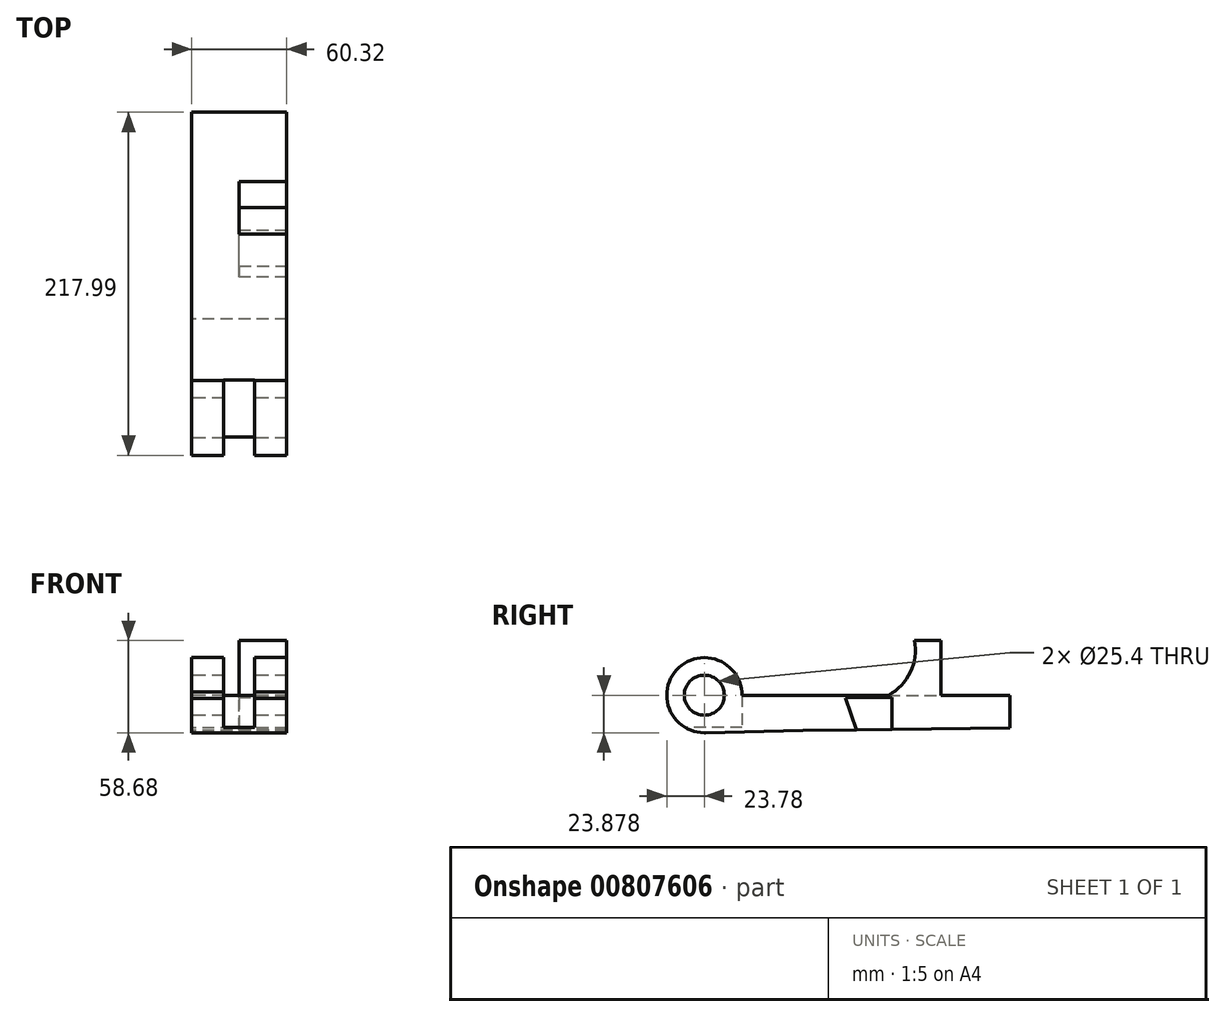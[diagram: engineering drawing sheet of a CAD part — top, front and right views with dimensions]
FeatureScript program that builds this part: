
annotation { "Feature Type Name" : "Feature", "Feature Type Description" : "" }
export const myFeature = defineFeature(function(context is Context, id is Id, definition is map)
    precondition{}
    {
        {
            var Q0;
            Q0=qCreatedBy(makeId("Right.planeOp"),FACE);
            var sketch = newSketch(context, id + "F0", { "sketchPlane" : qUnion([Q0])});
            skLineSegment(sketch, "E0.top", {"start": v(23.88, 20.58) * mm, "end": v(62.76, 20.58) * mm});
            skPoint(sketch, "E1.center.orphan", {"position": v(0, 10.29) * mm});
            skCircle(sketch, "E2", {"center": v(0, 20.58) * mm, "radius": 12.7 * mm});
            skArc(sketch, "E3", {"start": v(23.88, 20.58) * mm, "mid": v(-17.09, 37.25) * mm, "end": v(0.58, -3.3) * mm});
            skLineSegment(sketch, "E4", {"start": v(62.76, -1.77) * mm, "end": v(0, -3.3) * mm});
            skPoint(sketch, "E5.orphan", {"position": v(0, 0) * mm});
            skLineSegment(sketch, "E6", {"start": v(0, 10.29) * mm, "end": v(0, 7.88) * mm});
            skLineSegment(sketch, "E7", {"start": v(117.25, -0.45) * mm, "end": v(117.25, 20.58) * mm});
            skLineSegment(sketch, "E8.trimOffspring", {"start": v(0, -3.3) * mm, "end": v(0, -3.3) * mm});
            skLineSegment(sketch, "E9", {"start": v(0, 20.58) * mm, "end": v(85.85, 20.58) * mm});
            skLineSegment(sketch, "E10", {"start": v(85.85, 20.58) * mm, "end": v(91.86, -1.06) * mm});
            skLineSegment(sketch, "E11.bottom", {"start": v(85.85, 20.58) * mm, "end": v(150.21, 20.58) * mm});
            skLineSegment(sketch, "E11.top", {"start": v(133.54, 55.38) * mm, "end": v(150.21, 55.38) * mm});
            skLineSegment(sketch, "E11.right", {"start": v(150.21, 20.58) * mm, "end": v(150.21, 55.38) * mm});
            skPoint(sketch, "E12.startSnap0", {"position": v(133.54, 55.38) * mm});
            skArc(sketch, "E13", {"start": v(116.86, 20.58) * mm, "mid": v(130.87, 35.26) * mm, "end": v(133.54, 55.38) * mm});
            skPoint(sketch, "E12.start.orphan", {"position": v(133.54, 50.81) * mm});
            skPoint(sketch, "E14.orphan", {"position": v(116.87, 55.38) * mm});
            skLineSegment(sketch, "E15.bottom", {"start": v(23.78, -8.26) * mm, "end": v(-23.78, -8.26) * mm});
            skLineSegment(sketch, "E15.top", {"start": v(23.78, 49.42) * mm, "end": v(-23.78, 49.42) * mm});
            skLineSegment(sketch, "E15.left", {"start": v(23.78, -8.26) * mm, "end": v(23.78, 49.42) * mm});
            skLineSegment(sketch, "E15.right", {"start": v(-23.78, -8.26) * mm, "end": v(-23.78, 49.42) * mm});
            skLineSegment(sketch, "E16", {"start": v(62.76, -1.77) * mm, "end": v(194.2, -0.17) * mm});
            skLineSegment(sketch, "E17", {"start": v(194.2, -0.17) * mm, "end": v(194.2, 20.58) * mm});
            skLineSegment(sketch, "E18", {"start": v(150.21, 20.58) * mm, "end": v(194.2, 20.58) * mm});
            skPoint(sketch, "E19.start.orphan", {"position": v(0, -28.73) * mm});
            skPoint(sketch, "E20.orphan", {"position": v(208.3, 0) * mm});
            skSolve(sketch);
        }
        {
            var Q0;
            Q0=makeQuery(id+"F0.imprint","IMPRINT",FACE,{"disambiguationData":[TD([[makeQuery(id+"F0.imprint","IMPRINT",EDGE,{"derivedFrom":sQuery(id+"F0.wireOp",EDGE,"E11.top")}),-1.0]])]});
            extrude(context, id + "F1", {"entities" : qUnion([Q0]), "depth" : 30.16 * mm, "offsetDistance" : 25.4 * mm});
        }
        {
            var Q0;
            {var subQ5=sQuery(id+"F0.wireOp",EDGE,"E2");var subQ6=makeQuery(id+"F0.imprint","IMPRINT",VERTEX,{"disambiguationData":[OD(0.0)],"derivedFrom":subQ5});Q0=makeQuery(id+"F0.imprint","IMPRINT",FACE,{"disambiguationData":[TD([[makeQuery(id+"F0.imprint","IMPRINT",EDGE,{"disambiguationData":[TD([[subQ6,1.0]])],"derivedFrom":subQ5}),-1.0]])]});}
            var Q1;
            {var subQ9=sQuery(id+"F0.wireOp",EDGE,"E16");Q1=makeQuery(id+"F0.imprint","IMPRINT",FACE,{"disambiguationData":[TD([[makeQuery(id+"F0.imprint","IMPRINT",EDGE,{"derivedFrom":subQ9}),1.0]])]});}
            extrude(context, id + "F2", {"entities" : qUnion([Q0, Q1]), "operationType" : NewBodyOperationType.ADD, "endBound" : BoundingType.SYMMETRIC, "depth" : 60.32 * mm, "offsetDistance" : 25.4 * mm});
        }
        {
            var Q0;
            Q0=qCreatedBy(makeId("Right.planeOp"),FACE);
            var sketch = newSketch(context, id + "F3", { "sketchPlane" : qUnion([Q0])});
            skLineSegment(sketch, "E21", {"start": v(119.06, 19.17) * mm, "end": v(119.06, -2.56) * mm});
            skLineSegment(sketch, "E22", {"start": v(119.06, -2.56) * mm, "end": v(96.88, -2.56) * mm});
            skLineSegment(sketch, "E23", {"start": v(96.88, -2.56) * mm, "end": v(89.48, 18.92) * mm});
            skLineSegment(sketch, "E24", {"start": v(89.48, 18.92) * mm, "end": v(119.06, 19.17) * mm});
            skSolve(sketch);
        }
        {
            var Q0;
            Q0 = qSketchRegion(id + "F3", true);
            var Q1;
            {var subQ0=sQuery(id+"F0.wireOp",EDGE,"E11.bottom");Q1=makeQuery(id+"F2.boolean.opBoolean","MERGE",FACE,{"derivedFrom":[makeQuery(id+"F1.opExtrude","CAP_FACE",FACE,{"disambiguationData":[OSD([subQ0,sQuery(id+"F0.wireOp",EDGE,"E11.top"),sQuery(id+"F0.wireOp",EDGE,"E11.right"),sQuery(id+"F0.wireOp",EDGE,"E13")])],"isStart":false}),makeQuery(id+"F2.opExtrude","CAP_FACE",FACE,{"disambiguationData":[OSD([sQuery(id+"F0.wireOp",EDGE,"E2"),sQuery(id+"F0.wireOp",EDGE,"E3"),sQuery(id+"F0.wireOp",EDGE,"E4"),sQuery(id+"F0.wireOp",EDGE,"E9"),subQ0,sQuery(id+"F0.wireOp",EDGE,"E15.left"),sQuery(id+"F0.wireOp",EDGE,"E15.right"),sQuery(id+"F0.wireOp",EDGE,"E16"),sQuery(id+"F0.wireOp",EDGE,"E17"),sQuery(id+"F0.wireOp",EDGE,"E18")])],"isStart":false})]});}
            extrude(context, id + "F4", {"entities" : qUnion([Q0, Q1]), "operationType" : NewBodyOperationType.REMOVE, "depth" : 127.78 * mm, "offsetDistance" : 25.4 * mm});
        }
        {
            var Q0;
            {var subQ5=sQuery(id+"F0.wireOp",EDGE,"E15.top");Q0=makeQuery(id+"F0.imprint","IMPRINT",FACE,{"disambiguationData":[TD([[makeQuery(id+"F0.imprint","IMPRINT",EDGE,{"derivedFrom":subQ5}),1.0]])]});}
            var Q1;
            {var subQ3=sQuery(id+"F0.wireOp",EDGE,"E8.trimOffspring");Q1=makeQuery(id+"F0.imprint","IMPRINT",FACE,{"disambiguationData":[TD([[makeQuery(id+"F0.imprint","IMPRINT",EDGE,{"derivedFrom":subQ3}),-1.0]])]});}
            extrude(context, id + "F5", {"entities" : qUnion([Q0, Q1]), "operationType" : NewBodyOperationType.REMOVE, "endBound" : BoundingType.SYMMETRIC, "oppositeDirection" : true, "depth" : 346.27 * mm, "offsetDistance" : 25.4 * mm});
        }
        {
            var Q0;
            {var subQ5=sQuery(id+"F0.wireOp",EDGE,"E15.top");Q0=makeQuery(id+"F0.imprint","IMPRINT",FACE,{"disambiguationData":[TD([[makeQuery(id+"F0.imprint","IMPRINT",EDGE,{"derivedFrom":subQ5}),1.0]])]});}
            var Q1;
            {var subQ3=sQuery(id+"F0.wireOp",EDGE,"E8.trimOffspring");Q1=makeQuery(id+"F0.imprint","IMPRINT",FACE,{"disambiguationData":[TD([[makeQuery(id+"F0.imprint","IMPRINT",EDGE,{"derivedFrom":subQ3}),-1.0]])]});}
            extrude(context, id + "F6", {"entities" : qUnion([Q0, Q1]), "operationType" : NewBodyOperationType.REMOVE, "oppositeDirection" : true, "depth" : 109.44 * mm, "offsetDistance" : 25.4 * mm});
        }
        {
            var Q0;
            Q0=qCreatedBy(makeId("Top.planeOp"),FACE);
            var sketch = newSketch(context, id + "F7", { "sketchPlane" : qUnion([Q0])});
            skLineSegment(sketch, "E25.bottom", {"start": v(-9.82, 23.97) * mm, "end": v(9.95, 23.97) * mm});
            skLineSegment(sketch, "E25.top", {"start": v(-9.82, -23.88) * mm, "end": v(9.95, -23.88) * mm});
            skLineSegment(sketch, "E25.left", {"start": v(-9.82, 23.97) * mm, "end": v(-9.82, -23.88) * mm});
            skLineSegment(sketch, "E25.right", {"start": v(9.95, 23.97) * mm, "end": v(9.95, -23.88) * mm});
            skSolve(sketch);
        }
        {
            var Q0;
            Q0 = qSketchRegion(id + "F7", true);
            extrude(context, id + "F8", {"entities" : qUnion([Q0]), "operationType" : NewBodyOperationType.REMOVE, "depth" : 61.78 * mm, "offsetDistance" : 25.4 * mm});
        }
    });
